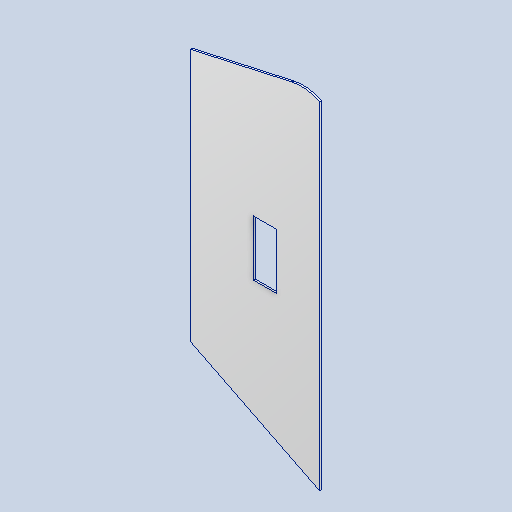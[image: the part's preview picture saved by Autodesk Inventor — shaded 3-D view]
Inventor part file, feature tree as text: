
AUTODESK INVENTOR PART (.ipt)
format: ipt  version: 2023 (Build 270158000, 158)  size: 126,976 bytes
history: native  units: mm
features: other x6, reference x5, extrude x2, sketch x2, projected_geometry x1
ambient origin geometry x8: Origin, YZ Plane, XZ Plane, XY Plane, X Axis, Y Axis, Z Axis, Center Point
bodies: Solid1 (feature_tree)
feature tree (16):
  extrude  "Extrusion1"  Depth=0.5mm TaperAngle=0.0deg
  extrude  "Extrusion2"  Depth=0.5mm
  sketch  "Sketch1"  dims[d0=0.5mm d1=0.0mm d2=0.5mm d3=0.0mm]
  reference  "Reference1"
  reference  "Reference2"
  reference  "Reference3"
  reference  "Reference4"
  reference  "Reference5"
  sketch  "Sketch2"  dims[d4=0.5mm d5=0.872665mm]
  projected_geometry  "Projected Loop1"
  other  "Assembly2"
  other  "sciana_lewa_v3:1"
  other  "pług:1"
  other  "pokrywa:1"
  other  "minisumopodsr:1"
  other  "koło_minisumo:1"
